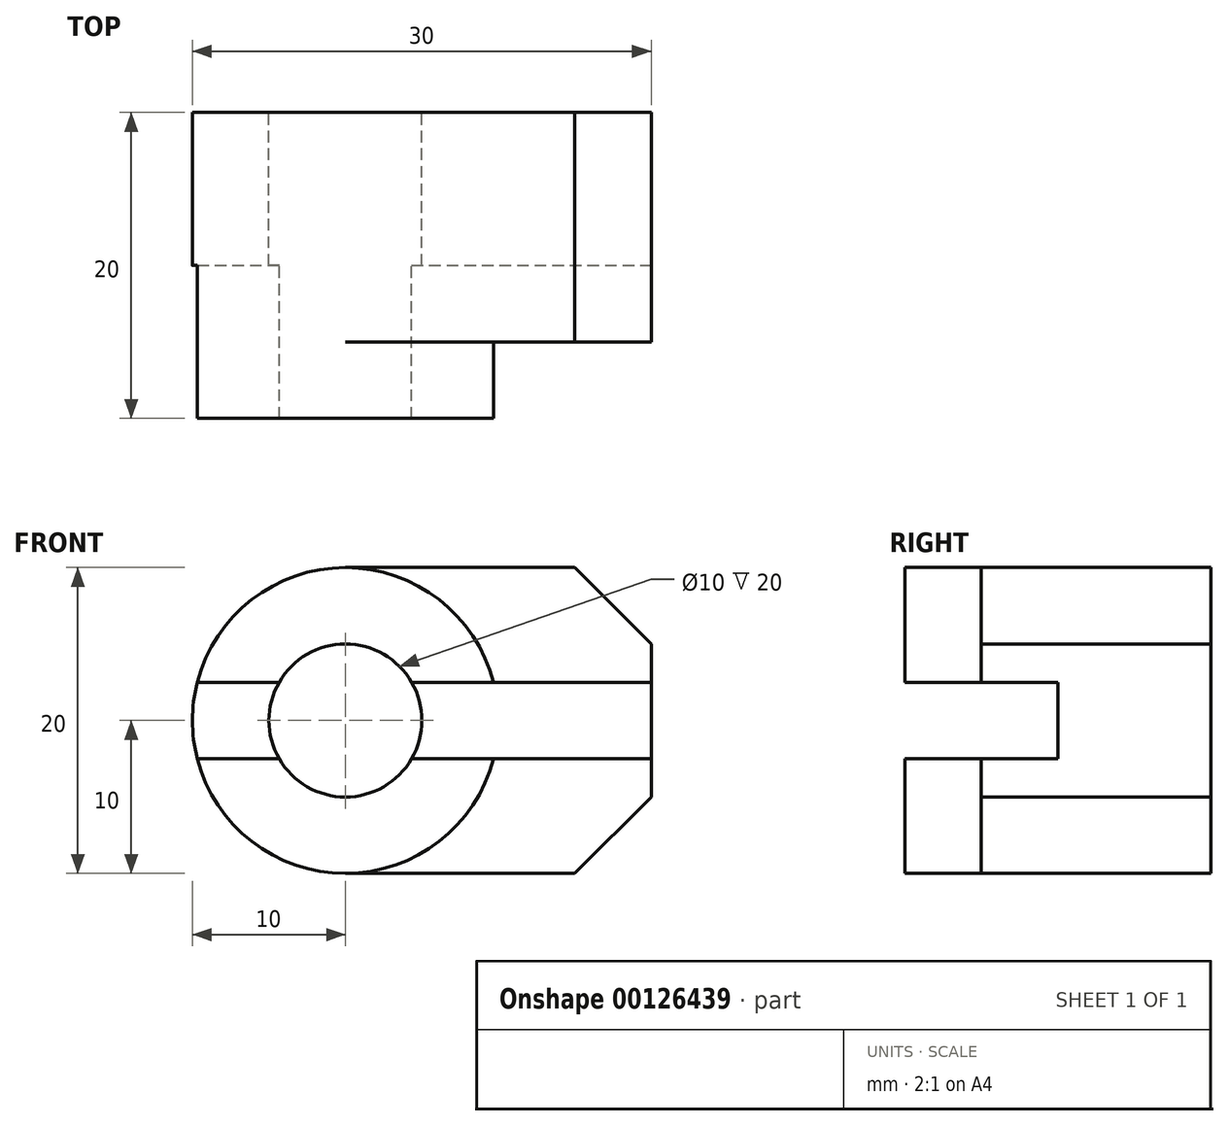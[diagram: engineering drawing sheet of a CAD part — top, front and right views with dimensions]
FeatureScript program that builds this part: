
annotation { "Feature Type Name" : "Feature", "Feature Type Description" : "" }
export const myFeature = defineFeature(function(context is Context, id is Id, definition is map)
    precondition{}
    {
        {
            var Q0;
            Q0=qCreatedBy(makeId("Front.planeOp"),FACE);
            var sketch = newSketch(context, id + "F0", { "sketchPlane" : qUnion([Q0])});
            skCircle(sketch, "E0", {"center": v(0, 0) * mm, "radius": 5 * mm});
            skCircle(sketch, "E1", {"center": v(0, 0) * mm, "radius": 10 * mm});
            skSolve(sketch);
        }
        {
            var Q0;
            Q0=qSketchRegion(id+"F0",true);
            extrude(context, id + "F1", {"entities" : qUnion([Q0]), "endBound" : BoundingType.SYMMETRIC, "depth" : 20 * mm});
        }
        {
            var Q0;
            Q0=makeQuery(id+"F1.opExtrude","CAP_FACE",FACE,{"disambiguationData":[OSD([sQuery(id+"F0.wireOp",EDGE,"E0"),sQuery(id+"F0.wireOp",EDGE,"E1")])],"isStart":true});
            var sketch = newSketch(context, id + "F2", { "sketchPlane" : qUnion([Q0])});
            skLineSegment(sketch, "E2", {"start": v(0, 0) * mm, "end": v(0, 10) * mm});
            skLineSegment(sketch, "E3", {"start": v(0, 10) * mm, "end": v(-15, 10) * mm});
            skLineSegment(sketch, "E4", {"start": v(-15, -10) * mm, "end": v(0, -10) * mm});
            skLineSegment(sketch, "E5", {"start": v(0, -10) * mm, "end": v(0, 0) * mm});
            skLineSegment(sketch, "E6", {"start": v(-15, 10) * mm, "end": v(-20, 5) * mm});
            skLineSegment(sketch, "E7", {"start": v(-15, -10) * mm, "end": v(-20, -5) * mm});
            skLineSegment(sketch, "E8", {"start": v(-20, 5) * mm, "end": v(-20, -5) * mm});
            skSolve(sketch);
        }
        {
            var Q0;
            Q0=qSketchRegion(id+"F2",true);
            extrude(context, id + "F3", {"entities" : qUnion([Q0]), "operationType" : NewBodyOperationType.ADD, "oppositeDirection" : true, "depth" : 15 * mm});
        }
        {
            var Q0;
            Q0=makeQuery(id+"F0.imprint","IMPRINT",FACE,{"disambiguationData":[TD([[makeQuery(id+"F0.imprint","IMPRINT",EDGE,{"derivedFrom":sQuery(id+"F0.wireOp",EDGE,"E0")}),1.0]])]});
            extrude(context, id + "F4", {"entities" : qUnion([Q0]), "operationType" : NewBodyOperationType.REMOVE, "endBound" : BoundingType.SYMMETRIC, "oppositeDirection" : true, "depth" : 20 * mm});
        }
        {
            var Q0;
            Q0=qCreatedBy(makeId("Front.planeOp"),FACE);
            var sketch = newSketch(context, id + "F5", { "sketchPlane" : qUnion([Q0])});
            skLineSegment(sketch, "E9", {"start": v(0, 2.5) * mm, "end": v(-10, 2.5) * mm});
            skLineSegment(sketch, "E10", {"start": v(-10, 2.5) * mm, "end": v(-10, -2.5) * mm});
            skLineSegment(sketch, "E11", {"start": v(-10, -2.5) * mm, "end": v(20, -2.5) * mm});
            skLineSegment(sketch, "E12", {"start": v(0, 2.5) * mm, "end": v(20, 2.5) * mm});
            skLineSegment(sketch, "E13", {"start": v(20, 2.5) * mm, "end": v(20, -2.5) * mm});
            skSolve(sketch);
        }
        {
            var Q0;
            Q0=qSketchRegion(id+"F5",true);
            var Q1;
            Q1=makeQuery(id+"F1.opExtrude","CAP_FACE",FACE,{"disambiguationData":[OSD([sQuery(id+"F0.wireOp",EDGE,"E0"),sQuery(id+"F0.wireOp",EDGE,"E1")])],"isStart":false});
            extrude(context, id + "F6", {"entities" : qUnion([Q0]), "operationType" : NewBodyOperationType.REMOVE, "endBound" : BoundingType.UP_TO_SURFACE, "endBoundEntityFace" : qUnion([Q1]), "depth" : 25 * mm});
        }
    });
